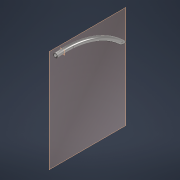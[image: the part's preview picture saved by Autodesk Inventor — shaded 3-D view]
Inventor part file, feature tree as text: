
AUTODESK INVENTOR PART (.ipt)
format: ipt  version: 2021 (Build 250183000, 183)  size: 277,504 bytes
history: native  units: mm
features: sketch x5, sweep x2, extrude x2, plane x2, split x1, hole x1
ambient origin geometry x8: Origin, YZ Plane, XZ Plane, XY Plane, X Axis, Y Axis, Z Axis, Center Point
bodies: Solid1 (feature_tree)
feature tree (13):
  sketch  "Sketch1"  dims[d0=3300.0mm d1=1650.0mm]
  sweep  "Sweep1"
  sweep  "Sweep2"
  extrude  "Extrusion1"  Depth=70.0mm
  extrude  "Extrusion3"  Depth=1650.0mm
  plane  "Work Plane1"
  split  "Split1"
  plane  "Work Plane2"
  hole  "Hole1"  [1 undecoded]
  sketch  "Sketch2"  dims[d2=0.0mm d3=80.0mm]
  sketch  "Sketch3"  dims[d4=0.0mm d5=0.0mm d6=70.0mm]
  sketch  "Sketch4"  dims[d7=0.0mm d8=1650.0mm]
  sketch  "Sketch7"  dims[d9=0.0mm d10=0.0mm d11=1810.0mm d12=3460.0mm d13=1730.0mm d14=1200.0mm d15=1730.0mm d16=1730.0mm d17=200.0mm d18=80.0mm d19=0.0mm d22=14.0mm d23=0.0mm d24=-144.0mm d25=-55.75mm d26=10.0mm d27=6.0mm d28=4.0mm d29=2.0mm d30=90.0deg d31=8.0mm d32=20.594885mm]
note: 1 required parameter value undecoded (feature->parameter linkage not recoverable at this tier; creation-order binding heuristic only, values carry confidence <= 0.55)
